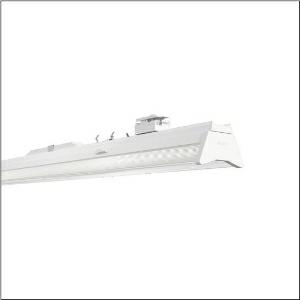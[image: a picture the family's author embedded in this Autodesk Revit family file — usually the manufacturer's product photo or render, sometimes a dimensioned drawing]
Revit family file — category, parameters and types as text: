
# Revit family: licross_r__11_performance_mo_51tm16mn4axg_6102
name_source: partatom
category: Lighting Fixtures
units: mm (PartAtom-declared; Revit-internal decimal feet)

## family parameters
Cut with Voids When Loaded = No
Host = Face
Light Source = No
Part Type = Normal
Room Calculation Point = No
Round Connector Dimension = Use Diameter
Shared = No

## types (1)
- --- (1 x LED, 10160 lm, 55.3 W, 4000K)
    Apparent Load = 55 VA
    CIE Flux Codes = 66 88 96 79 100
    Color Rendering = 80
    Color Temperature = 4000K
    Default Elevation = 1800 mm
    Description = Licross® 11 Performance MO, luminaire insert, of sheet steel, galvanised, coil coated, white, length: 1.500mm, width: 120mm, height: 123mm, LED rated luminous flux: 10.160lm, light colour: 840, control gear: ON/OFF Multilumen, with plug, 3-pole, with phase selection, mains connection: 220..240V, AC, 50/60Hz, rated input power: 55W, halogen-free wiring, primary light control with lens, of plastic, primary optical cover: cover, of PMMA, light emission: direct/indirect distribution, primary light characteristic: symmetric, protection rating (complete): IP40, insulation class (complete): insulation class I (protective earthing), certification: CE, ENEC, VDE, UKCA, protection symbol: D if used in an environment without relevant dust loads with corresponding accessories, impact resistance: IK06, permissible ambient temperature for indoor applications: -35..+40°C, corresponds to IFS (International Featured Standards) requirements for safety and quality in the food industry, reducing of maximum allowable ambient temperature of 5°C with ceiling mounting, LABS conformity tested according to VDMA 24364:2018-05, packaging unit: 1 piece
    Height = 114 mm
    Lamp = 1 x LED
    Lamp Light Flux = 10160 lm
    Lamp Power = 55.3 W
    Lamp count = 1
    Length = 1500 mm
    Luminous efficacy = 184 lm/W
    Manufacturer = Siteco
    ModVariant = No
    Model = 51TM16MN4AXG
    Mounting Place = Ceiling
    Mounting Type = Pendant
    Number of Poles = 1
    OnlyDefault = Yes
    Power Factor = 1
    Product Name = Licross® 11 Performance MO
    Product group = luminaire insert
    ProductGroupID = 902
    Protection Class = Protection class I
    Protection Degree = IP 40
    RLX_Detail_Level = 1
    RLX_Emergency_Light_Flux = 0 lm
    RLX_Emergency_Type = 0
    RLX_Emergency_Type_DB = No
    RlxData = <blob elided: 31793 chars, md5=b826379e>
    Socket = socket
    Standby Power = 0 W
    System Light Flux = 10160 lm
    System Power = 55 W
    Type Comments = factory setting: luminous flux: 100 % | (A | C | E) | 126 mA
    Type Image = l_1256138.jpg
    URL = http://relux.com
    VarID = @adj_086122
    Voltage = 0 V
    Weight = 0.00 kg
    Width = 120 mm

## geometry (parser evidence)
native form markers: Blend x4, Sweep x12
no freeform markers — native parametric forms only
